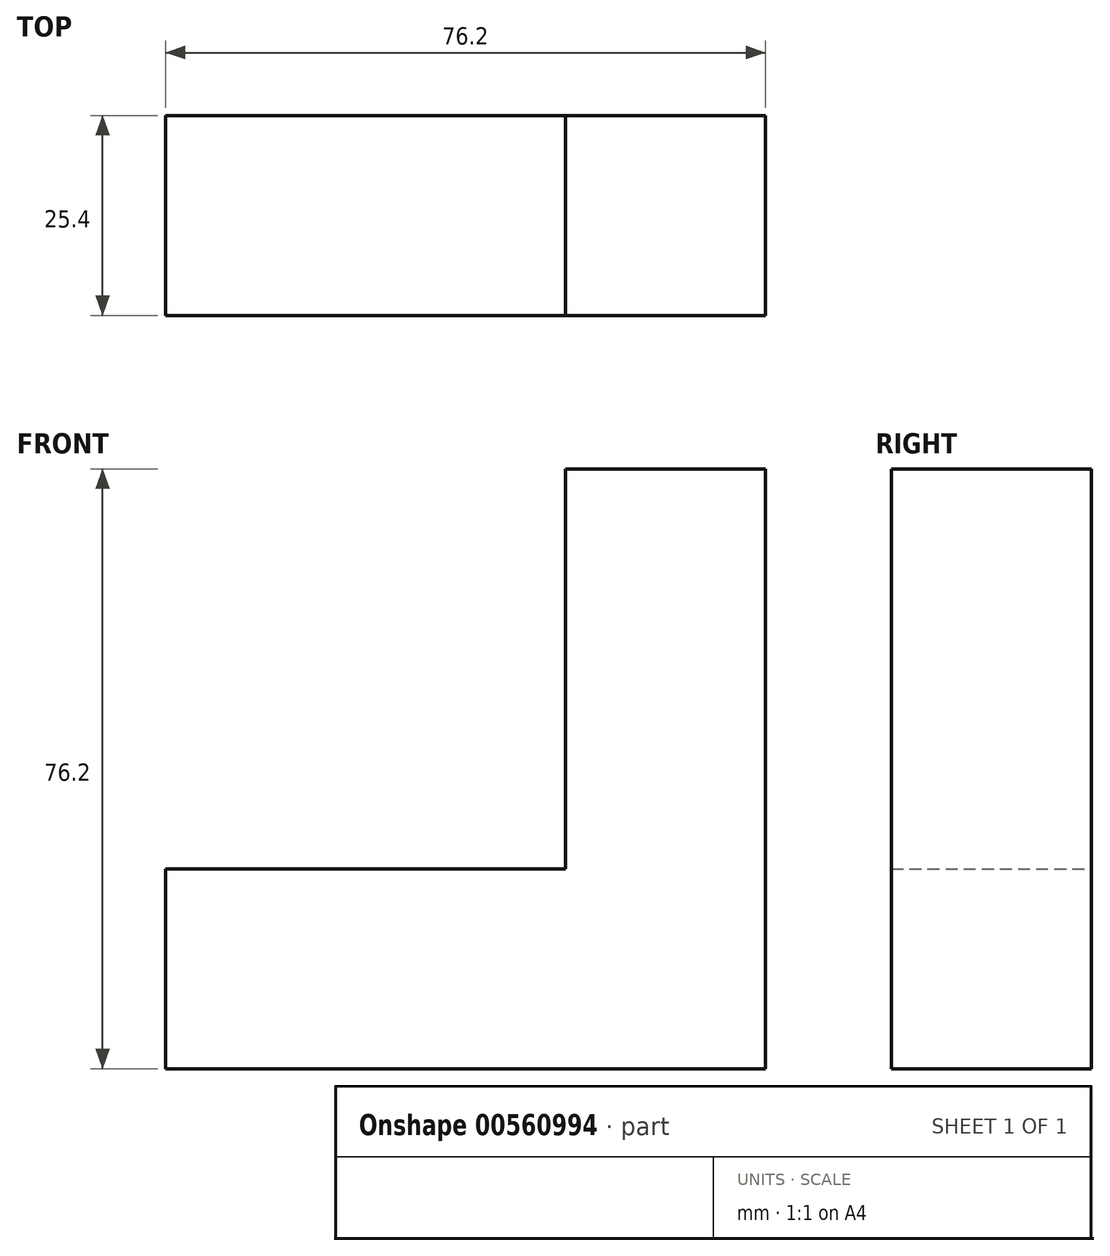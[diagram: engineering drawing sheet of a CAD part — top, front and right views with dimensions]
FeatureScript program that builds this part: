
annotation { "Feature Type Name" : "Feature", "Feature Type Description" : "" }
export const myFeature = defineFeature(function(context is Context, id is Id, definition is map)
    precondition{}
    {
        {
            var Q0;
            Q0=qCreatedBy(makeId("Front.planeOp"),FACE);
            var sketch = newSketch(context, id + "F0", { "sketchPlane" : qUnion([Q0])});
            skLineSegment(sketch, "E0.bottom", {"start": v(0, 0) * mm, "end": v(25.4, 0) * mm});
            skLineSegment(sketch, "E0.top", {"start": v(0, 25.4) * mm, "end": v(25.4, 25.4) * mm});
            skLineSegment(sketch, "E0.left", {"start": v(0, 0) * mm, "end": v(0, 25.4) * mm});
            skLineSegment(sketch, "E0.right", {"start": v(25.4, 0) * mm, "end": v(25.4, 25.4) * mm});
            skLineSegment(sketch, "E1.bottom", {"start": v(0, 25.4) * mm, "end": v(-25.4, 25.4) * mm});
            skLineSegment(sketch, "E1.top", {"start": v(0, 0) * mm, "end": v(-25.4, 0) * mm});
            skLineSegment(sketch, "E1.left", {"start": v(0, 25.4) * mm, "end": v(0, 0) * mm});
            skLineSegment(sketch, "E1.right", {"start": v(-25.4, 25.4) * mm, "end": v(-25.4, 0) * mm});
            skLineSegment(sketch, "E2.bottom", {"start": v(-25.4, 25.4) * mm, "end": v(-50.8, 25.4) * mm});
            skLineSegment(sketch, "E2.top", {"start": v(-25.4, 0) * mm, "end": v(-50.8, 0) * mm});
            skLineSegment(sketch, "E2.right", {"start": v(-50.8, 25.4) * mm, "end": v(-50.8, 0) * mm});
            skLineSegment(sketch, "E3.bottom", {"start": v(-50.8, 25.4) * mm, "end": v(-25.4, 25.4) * mm});
            skLineSegment(sketch, "E3.top", {"start": v(-50.8, 50.8) * mm, "end": v(-25.4, 50.8) * mm});
            skLineSegment(sketch, "E3.left", {"start": v(-50.8, 25.4) * mm, "end": v(-50.8, 50.8) * mm});
            skLineSegment(sketch, "E3.right", {"start": v(-25.4, 25.4) * mm, "end": v(-25.4, 50.8) * mm});
            skLineSegment(sketch, "E4.top", {"start": v(0, 50.8) * mm, "end": v(25.4, 50.8) * mm});
            skLineSegment(sketch, "E4.left", {"start": v(0, 25.4) * mm, "end": v(0, 50.8) * mm});
            skLineSegment(sketch, "E4.right", {"start": v(25.4, 25.4) * mm, "end": v(25.4, 50.8) * mm});
            skLineSegment(sketch, "E5.top", {"start": v(0, 76.2) * mm, "end": v(25.4, 76.2) * mm});
            skLineSegment(sketch, "E5.left", {"start": v(0, 50.8) * mm, "end": v(0, 76.2) * mm});
            skLineSegment(sketch, "E5.right", {"start": v(25.4, 50.8) * mm, "end": v(25.4, 76.2) * mm});
            skSolve(sketch);
        }
        {
            var Q0;
            Q0=makeQuery(id+"F0.imprint","IMPRINT",FACE,{"disambiguationData":[TD([[makeQuery(id+"F0.imprint","IMPRINT",EDGE,{"derivedFrom":sQuery(id+"F0.wireOp",EDGE,"E3.bottom")}),1.0]])]});
            var Q1;
            Q1=makeQuery(id+"F0.imprint","IMPRINT",FACE,{"disambiguationData":[TD([[makeQuery(id+"F0.imprint","IMPRINT",EDGE,{"derivedFrom":sQuery(id+"F0.wireOp",EDGE,"E2.top")}),-1.0]])]});
            var Q2;
            Q2=makeQuery(id+"F0.imprint","IMPRINT",FACE,{"disambiguationData":[TD([[makeQuery(id+"F0.imprint","IMPRINT",EDGE,{"derivedFrom":sQuery(id+"F0.wireOp",EDGE,"E1.bottom")}),1.0]])]});
            var Q3;
            Q3=makeQuery(id+"F0.imprint","IMPRINT",FACE,{"disambiguationData":[TD([[makeQuery(id+"F0.imprint","IMPRINT",EDGE,{"derivedFrom":sQuery(id+"F0.wireOp",EDGE,"E0.bottom")}),1.0]])]});
            var Q4;
            Q4=makeQuery(id+"F0.imprint","IMPRINT",FACE,{"disambiguationData":[TD([[makeQuery(id+"F0.imprint","IMPRINT",EDGE,{"derivedFrom":sQuery(id+"F0.wireOp",EDGE,"E0.top")}),1.0]])]});
            var Q5;
            Q5=makeQuery(id+"F0.imprint","IMPRINT",FACE,{"disambiguationData":[TD([[makeQuery(id+"F0.imprint","IMPRINT",EDGE,{"derivedFrom":sQuery(id+"F0.wireOp",EDGE,"E4.top")}),1.0]])]});
            extrude(context, id + "F1", {"entities" : qUnion([Q0, Q1, Q2, Q3, Q4, Q5]), "depth" : 25.4 * mm, "offsetDistance" : 25.4 * mm});
        }
    });
